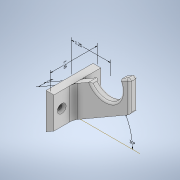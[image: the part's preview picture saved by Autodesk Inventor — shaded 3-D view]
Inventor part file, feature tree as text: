
AUTODESK INVENTOR PART (.ipt)
format: ipt  version: 2021.1 (Build 251245010, 245A)  size: 403,968 bytes
history: native  units: in
note: dims shown in document units (in); Inventor stores cm internally (conversion verified against a paired STEP export)
features: other x5, sketch x5, extrude x4, fillet x4, hole x1
ambient origin geometry x8: Origin, YZ Plane, XZ Plane, XY Plane, X Axis, Y Axis, Z Axis, Center Point
bodies: Solid2 (feature_tree)
feature tree (19):
  other  "Annotations"
  extrude  "Extrusion3"  Depth=0.25in
  extrude  "Extrusion4"  TaperAngle=30.0deg  [1 undecoded]
  sketch  "Sketch7"  dims[d26=1.075in d29=0.25in]
  extrude  "Extrusion5"  Depth=0.25in
  hole  "Hole3"  [1 undecoded]
  fillet  "Fillet3"  [1 undecoded]
  fillet  "Fillet4"  [1 undecoded]
  fillet  "Fillet5"  Radius=0.25in
  fillet  "Fillet6"  Radius=0.25in
  extrude  "Extrusion6"  Depth=0.0625in
  sketch  "Sketch5"  dims[d21=1.0in d22=0.25in]
  sketch  "Sketch6"  dims[d23=1.5in d24=0.0in d25=30.0deg]
  sketch  "Sketch8"  dims[d30=1.25in d31=0.25in d32=0.0in d33=0.0in d34=0.25in d35=0.25in]
  sketch  "Sketch9"  dims[d47=1.5in d48=0.0in d49=0.15in d50=0.75in d51=0.279in d52=0.25in d53=0.5635in d54=1.0in d55=0.8108in d65=0.0625in d66=0.0625in d67=0.0625in d68=0.125in d72=0.05in d73=0.0in d56=0.2085in d57=0.331in d58=1.5in d59=2.3174in d60=30.0deg d69=1.25in d70=0.3005in d71=0.25in]
  other  "Linear Dimension 1"
  other  "Angular Dimension 1"
  other  "Linear Dimension 2"
  other  "Linear Dimension 3"
note: 4 required parameter values undecoded (feature->parameter linkage not recoverable at this tier; creation-order binding heuristic only, values carry confidence <= 0.55)
